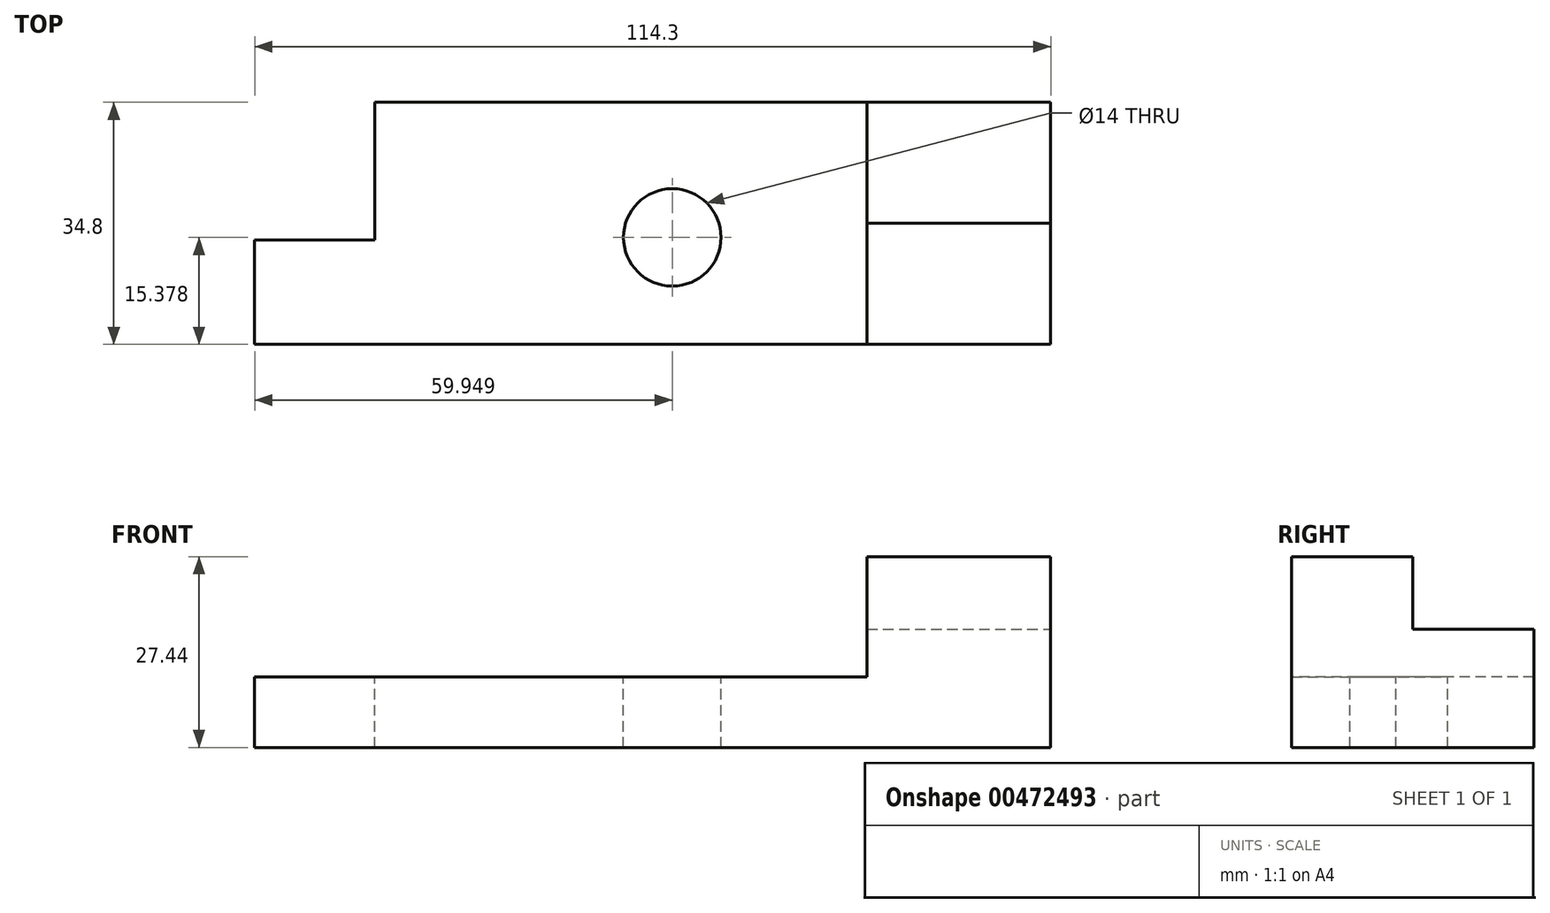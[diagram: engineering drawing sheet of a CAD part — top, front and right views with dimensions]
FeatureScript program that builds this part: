
annotation { "Feature Type Name" : "Feature", "Feature Type Description" : "" }
export const myFeature = defineFeature(function(context is Context, id is Id, definition is map)
    precondition{}
    {
        {
            var Q0;
            Q0=qCreatedBy(makeId("Front.planeOp"),FACE);
            var sketch = newSketch(context, id + "F0", { "sketchPlane" : qUnion([Q0])});
            skLineSegment(sketch, "E0", {"start": v(-51.08, 0) * mm, "end": v(63.22, 0) * mm});
            skLineSegment(sketch, "E1", {"start": v(63.22, 0) * mm, "end": v(-51.08, 0) * mm});
            skLineSegment(sketch, "E2", {"start": v(-51.08, 0) * mm, "end": v(-51.08, 10.17) * mm});
            skLineSegment(sketch, "E3", {"start": v(-51.08, 10.17) * mm, "end": v(63.22, 10.17) * mm});
            skLineSegment(sketch, "E4", {"start": v(63.22, 10.17) * mm, "end": v(63.22, 0) * mm});
            skSolve(sketch);
        }
        {
            var Q0;
            Q0=qSketchRegion(id+"F0",true);
            extrude(context, id + "F1", {"entities" : qUnion([Q0]), "depth" : 34.8 * mm});
        }
        {
            var Q0;
            Q0=makeQuery(id+"F1.opExtrude","SWEPT_FACE",FACE,{"disambiguationData":[OSD([sQuery(id+"F0.wireOp",EDGE,"E3")])]});
            var sketch = newSketch(context, id + "F2", { "sketchPlane" : qUnion([Q0])});
            skLineSegment(sketch, "E5", {"start": v(-33.85, 0) * mm, "end": v(-33.85, -19.8) * mm});
            skLineSegment(sketch, "E6", {"start": v(-33.85, -19.8) * mm, "end": v(-51.08, -19.8) * mm});
            skLineSegment(sketch, "E7", {"start": v(-51.08, -19.8) * mm, "end": v(-51.08, 0) * mm});
            skSolve(sketch);
        }
        {
            var Q0;
            {var subQ0=sQuery(id+"F2.wireOp",EDGE,"E5");Q0=makeQuery(id+"F2.imprint","IMPRINT",FACE,{"disambiguationData":[TD([[makeQuery(id+"F2.imprint","IMPRINT",EDGE,{"derivedFrom":subQ0}),-1.0]])]});}
            extrude(context, id + "F3", {"entities" : qUnion([Q0]), "operationType" : NewBodyOperationType.REMOVE, "oppositeDirection" : true, "depth" : 25.4 * mm});
        }
        {
            var Q0;
            Q0=makeQuery(id+"F1.opExtrude","SWEPT_FACE",FACE,{"disambiguationData":[OSD([sQuery(id+"F0.wireOp",EDGE,"E3")])]});
            var sketch = newSketch(context, id + "F4", { "sketchPlane" : qUnion([Q0])});
            skCircle(sketch, "E8", {"center": v(8.87, -19.42) * mm, "radius": 7 * mm});
            skSolve(sketch);
        }
        {
            var Q0;
            Q0=qSketchRegion(id+"F4",true);
            extrude(context, id + "F5", {"entities" : qUnion([Q0]), "operationType" : NewBodyOperationType.REMOVE, "oppositeDirection" : true, "depth" : 25.4 * mm});
        }
        {
            var Q0;
            Q0=makeQuery(id+"F1.opExtrude","SWEPT_FACE",FACE,{"disambiguationData":[OSD([sQuery(id+"F0.wireOp",EDGE,"E3")])]});
            var sketch = newSketch(context, id + "F6", { "sketchPlane" : qUnion([Q0])});
            skLineSegment(sketch, "E9", {"start": v(63.22, 0) * mm, "end": v(36.84, 0) * mm});
            skLineSegment(sketch, "E10", {"start": v(36.84, 0) * mm, "end": v(36.84, -34.8) * mm});
            skLineSegment(sketch, "E11", {"start": v(36.84, -34.8) * mm, "end": v(63.22, -34.8) * mm});
            skLineSegment(sketch, "E12", {"start": v(63.22, -34.8) * mm, "end": v(63.22, 0) * mm});
            skSolve(sketch);
        }
        {
            var Q0;
            Q0=qSketchRegion(id+"F6",true);
            extrude(context, id + "F7", {"entities" : qUnion([Q0]), "operationType" : NewBodyOperationType.ADD, "depth" : 17.27 * mm});
        }
        {
            var Q0;
            Q0=makeQuery(id+"F7.opExtrude","CAP_FACE",FACE,{"disambiguationData":[OSD([sQuery(id+"F6.wireOp",EDGE,"E9"),sQuery(id+"F6.wireOp",EDGE,"E10"),sQuery(id+"F6.wireOp",EDGE,"E11"),sQuery(id+"F6.wireOp",EDGE,"E12")])],"isStart":false});
            var sketch = newSketch(context, id + "F8", { "sketchPlane" : qUnion([Q0])});
            skLineSegment(sketch, "E13", {"start": v(63.22, -17.4) * mm, "end": v(36.84, -17.4) * mm});
            skLineSegment(sketch, "E14", {"start": v(36.84, -17.4) * mm, "end": v(36.84, 0) * mm});
            skLineSegment(sketch, "E15", {"start": v(36.84, 0) * mm, "end": v(63.22, 0) * mm});
            skLineSegment(sketch, "E16", {"start": v(63.22, 0) * mm, "end": v(63.22, -17.4) * mm});
            skSolve(sketch);
        }
        {
            var Q0;
            Q0=qSketchRegion(id+"F8",true);
            extrude(context, id + "F9", {"entities" : qUnion([Q0]), "operationType" : NewBodyOperationType.REMOVE, "oppositeDirection" : true, "depth" : 10.4 * mm});
        }
    });
